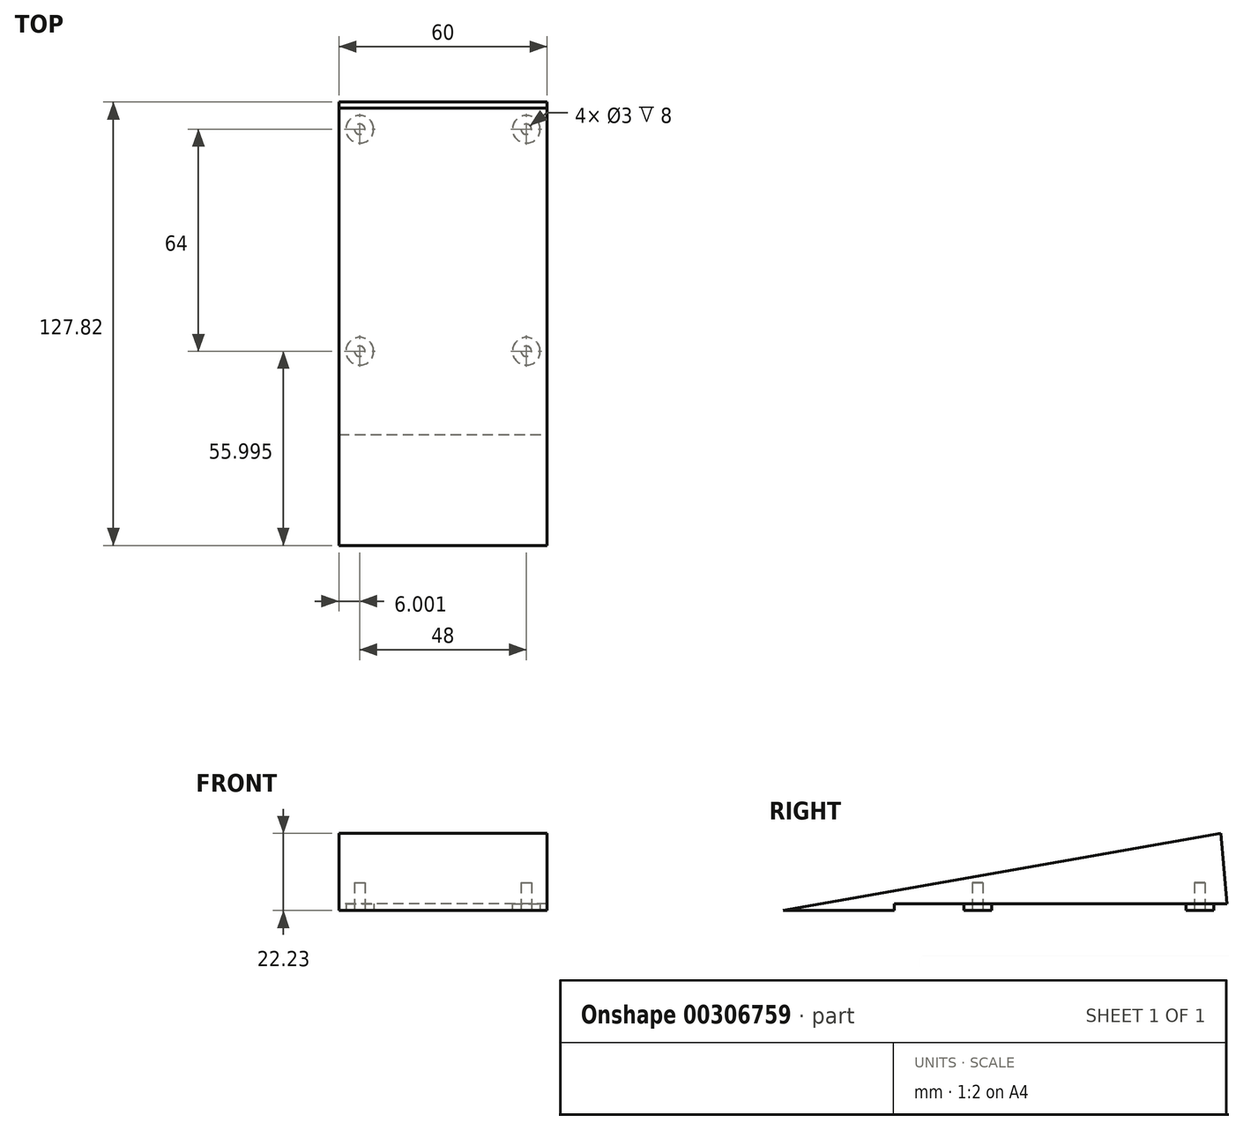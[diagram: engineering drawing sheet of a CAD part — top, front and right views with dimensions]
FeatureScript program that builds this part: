
annotation { "Feature Type Name" : "Feature", "Feature Type Description" : "" }
export const myFeature = defineFeature(function(context is Context, id is Id, definition is map)
    precondition{}
    {
        {
            var Q0;
            Q0=qCreatedBy(makeId("Top.planeOp"),FACE);
            var sketch = newSketch(context, id + "F0", { "sketchPlane" : qUnion([Q0])});
            skLineSegment(sketch, "E0.bottom", {"start": v(-34.04, 82.92) * mm, "end": v(25.96, 82.92) * mm});
            skLineSegment(sketch, "E0.top", {"start": v(-34.04, -45.08) * mm, "end": v(25.96, -45.08) * mm});
            skLineSegment(sketch, "E0.left", {"start": v(-34.04, 82.92) * mm, "end": v(-34.04, -45.08) * mm});
            skLineSegment(sketch, "E0.right", {"start": v(25.96, 82.92) * mm, "end": v(25.96, -45.08) * mm});
            skSolve(sketch);
        }
        {
            var Q0;
            Q0=makeQuery(id+"F0.imprint","IMPRINT",FACE,{"disambiguationData":[TD([[makeQuery(id+"F0.imprint","IMPRINT",EDGE,{"derivedFrom":sQuery(id+"F0.wireOp",EDGE,"E0.bottom")}),-1.0]])]});
            var Q1;
            Q1=sQuery(id+"F0.wireOp",EDGE,"E0.top");
            revolve(context, id + "F1", {"entities" : qUnion([Q0]), "axis" : qUnion([Q1]), "revolveType" : RevolveType.ONE_DIRECTION, "angle" : 10 * degree});
        }
        {
            var Q0;
            Q0=makeQuery(id+"F1.opRevolve","SWEPT_FACE",FACE,{"disambiguationData":[OSD([sQuery(id+"F0.wireOp",EDGE,"E0.right")])]});
            var sketch = newSketch(context, id + "F2", { "sketchPlane" : qUnion([Q0])});
            skLineSegment(sketch, "E1", {"start": v(82.92, 0) * mm, "end": v(80.97, 22.23) * mm});
            skSolve(sketch);
        }
        {
            var Q0;
            Q0=makeQuery(id+"F2.imprint","IMPRINT",FACE,{"disambiguationData":[TD([[makeQuery(id+"F2.imprint","IMPRINT",EDGE,{"derivedFrom":sQuery(id+"F2.wireOp",EDGE,"E1")}),-1.0]])]});
            extrude(context, id + "F3", {"entities" : qUnion([Q0]), "operationType" : NewBodyOperationType.REMOVE, "endBound" : BoundingType.THROUGH_ALL, "oppositeDirection" : true, "depth" : 25 * mm});
        }
        {
            var Q0;
            Q0=makeQuery(id+"F1.opRevolve","CAP_FACE",FACE,{"disambiguationData":[OSD([sQuery(id+"F0.wireOp",EDGE,"E0.bottom"),sQuery(id+"F0.wireOp",EDGE,"E0.top"),sQuery(id+"F0.wireOp",EDGE,"E0.left"),sQuery(id+"F0.wireOp",EDGE,"E0.right")])],"isStart":true});
            var sketch = newSketch(context, id + "F4", { "sketchPlane" : qUnion([Q0])});
            skLineSegment(sketch, "E2.bottom", {"start": v(-34.04, 13.08) * mm, "end": v(25.96, 13.08) * mm});
            skLineSegment(sketch, "E2.top", {"start": v(-34.04, -82.92) * mm, "end": v(25.96, -82.92) * mm});
            skLineSegment(sketch, "E2.left", {"start": v(-34.04, 13.08) * mm, "end": v(-34.04, -82.92) * mm});
            skLineSegment(sketch, "E2.right", {"start": v(25.96, 13.08) * mm, "end": v(25.96, -82.92) * mm});
            skCircle(sketch, "E3", {"center": v(-28.04, -74.92) * mm, "radius": 4 * mm});
            skCircle(sketch, "E4", {"center": v(-28.04, -74.92) * mm, "radius": 1.5 * mm});
            skCircle(sketch, "E5.0.1.0", {"center": v(-28.04, -10.92) * mm, "radius": 4 * mm});
            skCircle(sketch, "E5.1.0.0", {"center": v(19.96, -74.92) * mm, "radius": 4 * mm});
            skCircle(sketch, "E5.1.1.0", {"center": v(19.96, -10.92) * mm, "radius": 4 * mm});
            skLineSegment(sketch, "E5.direction1", {"start": v(-28.04, -74.92) * mm, "end": v(19.96, -74.92) * mm, "construction": true});
            skLineSegment(sketch, "E5.direction2", {"start": v(-28.04, -74.92) * mm, "end": v(-28.04, -10.92) * mm, "construction": true});
            skCircle(sketch, "E6.0.1.0", {"center": v(-28.04, -10.92) * mm, "radius": 1.5 * mm});
            skCircle(sketch, "E6.1.0.0", {"center": v(19.96, -74.92) * mm, "radius": 1.5 * mm});
            skCircle(sketch, "E6.1.1.0", {"center": v(19.96, -10.92) * mm, "radius": 1.5 * mm});
            skSolve(sketch);
        }
        {
            var Q0;
            Q0=makeQuery(id+"F4.imprint","IMPRINT",FACE,{"disambiguationData":[TD([[makeQuery(id+"F4.imprint","IMPRINT",EDGE,{"derivedFrom":sQuery(id+"F4.wireOp",EDGE,"E2.bottom")}),-1.0]])]});
            extrude(context, id + "F5", {"entities" : qUnion([Q0]), "operationType" : NewBodyOperationType.REMOVE, "oppositeDirection" : true, "depth" : 2 * mm});
        }
        {
            var Q0;
            Q0=makeQuery(id+"F4.imprint","IMPRINT",FACE,{"disambiguationData":[TD([[makeQuery(id+"F4.imprint","IMPRINT",EDGE,{"derivedFrom":sQuery(id+"F4.wireOp",EDGE,"E6.0.1.0")}),1.0]])]});
            var Q1;
            Q1=makeQuery(id+"F4.imprint","IMPRINT",FACE,{"disambiguationData":[TD([[makeQuery(id+"F4.imprint","IMPRINT",EDGE,{"derivedFrom":sQuery(id+"F4.wireOp",EDGE,"E6.1.1.0")}),1.0]])]});
            var Q2;
            Q2=makeQuery(id+"F4.imprint","IMPRINT",FACE,{"disambiguationData":[TD([[makeQuery(id+"F4.imprint","IMPRINT",EDGE,{"derivedFrom":sQuery(id+"F4.wireOp",EDGE,"E6.1.0.0")}),1.0]])]});
            var Q3;
            Q3=makeQuery(id+"F4.imprint","IMPRINT",FACE,{"disambiguationData":[TD([[makeQuery(id+"F4.imprint","IMPRINT",EDGE,{"derivedFrom":sQuery(id+"F4.wireOp",EDGE,"E4")}),1.0]])]});
            extrude(context, id + "F6", {"entities" : qUnion([Q0, Q1, Q2, Q3]), "operationType" : NewBodyOperationType.REMOVE, "oppositeDirection" : true, "depth" : 8 * mm});
        }
    });
